# Revit family: VTp751 уголок
name_source: partatom
category: Соединительные детали трубопроводов
revit_build: Autodesk Revit 2015 (Build: 20140606_1530(x64)
units: mm (PartAtom-declared; Revit-internal decimal feet)

## types (9) — shared parameters
Группа модели = VTp.700
Изготовитель = VALTEC S.R.L.
Коэффициент K = 0.5
Метод определения потерь = Коэффициент K
Описание = Угольник 90
Таблица коэффициентов K = Angle Valve Threaded

## per-type parameters (varying)
| type | 110 | 20 | 25 | 32 | 40 | 50 | 63 | 75 | 90 | A | B | d | Код по классификатору |
| 20 | Нет | Да | Нет | Нет | Нет | Нет | Нет | Нет | Нет | 26 мм | 15 мм | 20 мм | VTp.751.0.020 |
| 25 | Нет | Нет | Да | Нет | Нет | Нет | Нет | Нет | Нет | 30 мм | 17 мм | 25 мм | VTp.751.0.025 |
| 40 | Нет | Нет | Нет | Нет | Да | Нет | Нет | Нет | Нет | 45 мм | 21 мм | 40 мм | VTp.751.0.040 |
| 32 | Нет | Нет | Нет | Да | Нет | Нет | Нет | Нет | Нет | 36 мм | 19 мм | 32 мм | VTp.751.0.032 |
| 50 | Нет | Нет | Нет | Нет | Нет | Да | Нет | Нет | Нет | 53 мм | 24 мм | 50 мм | VTp.751.0.050 |
| 63 | Нет | Нет | Нет | Нет | Нет | Нет | Да | Нет | Нет | 68 мм | 26 мм | 63 мм | VTp.751.0.063 |
| 75 | Нет | Нет | Нет | Нет | Нет | Нет | Нет | Да | Нет | 75 мм | 30 мм | 75 мм | VTp.751.0.075 |
| 90 | Нет | Нет | Нет | Нет | Нет | Нет | Нет | Нет | Да | 89 мм | 33 мм | 90 мм | VTp.751.0.090 |
| 110 | Да | Нет | Нет | Нет | Нет | Нет | Нет | Нет | Нет | 105 мм | 37 мм | 110 мм | VTp.751.0.110 |
